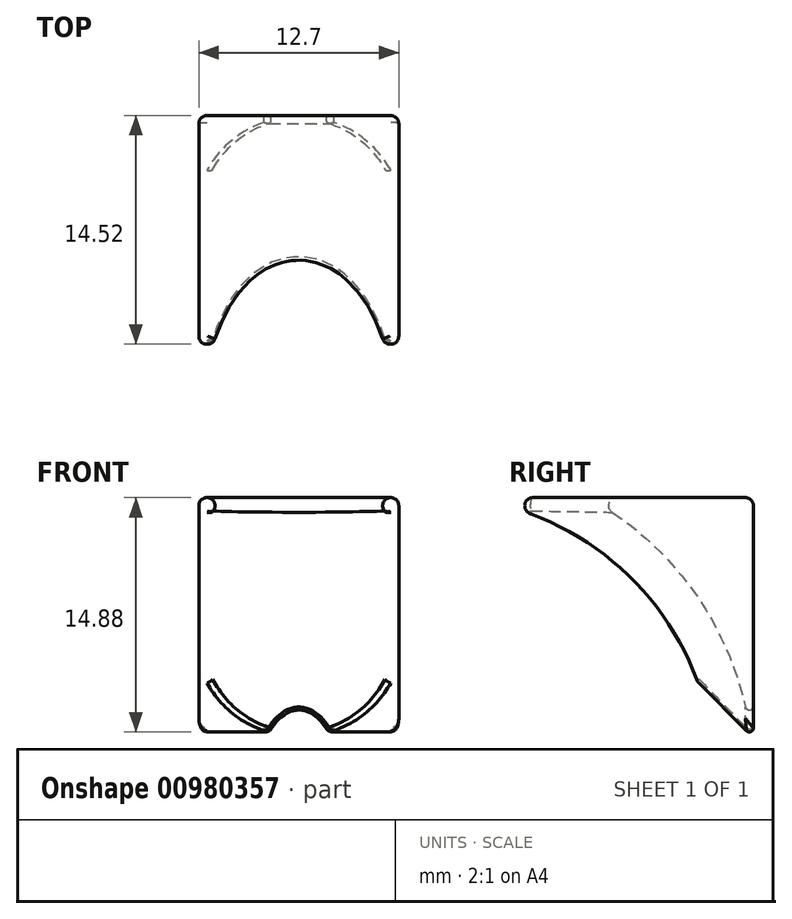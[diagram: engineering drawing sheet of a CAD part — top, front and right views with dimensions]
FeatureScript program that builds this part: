
annotation { "Feature Type Name" : "Feature", "Feature Type Description" : "" }
export const myFeature = defineFeature(function(context is Context, id is Id, definition is map)
    precondition{}
    {
        {
            var Q0;
            Q0=qCreatedBy(makeId("Right.planeOp"),FACE);
            var sketch = newSketch(context, id + "F0", { "sketchPlane" : qUnion([Q0])});
            skLineSegment(sketch, "E0", {"start": v(0, 0) * mm, "end": v(-15.24, 15.24) * mm});
            skLineSegment(sketch, "E1", {"start": v(-15.24, 15.24) * mm, "end": v(0, 15.24) * mm});
            skLineSegment(sketch, "E2", {"start": v(0, 15.24) * mm, "end": v(0, 0) * mm});
            skSolve(sketch);
        }
        {
            var Q0;
            Q0=makeQuery(id+"F0.imprint","IMPRINT",FACE,{"disambiguationData":[TD([[makeQuery(id+"F0.imprint","IMPRINT",EDGE,{"derivedFrom":sQuery(id+"F0.wireOp",EDGE,"E0")}),-1.0]])]});
            extrude(context, id + "F1", {"entities" : qUnion([Q0]), "endBound" : BoundingType.SYMMETRIC, "depth" : 12.7 * mm, "offsetDistance" : 25.4 * mm});
        }
        {
            var Q0;
            Q0=qCreatedBy(makeId("Top.planeOp"),FACE);
            cPlane(context, id + "F2", {"entities" : qUnion([Q0]), "cplaneType" : CPlaneType.OFFSET, "offset" : 2.54 * mm, "oppositeDirection" : true, "width" : 152.4 * mm, "height" : 152.4 * mm});
        }
        {
            var Q0;
            Q0=qCreatedBy(id+"F2.planeOp",FACE);
            var sketch = newSketch(context, id + "F3", { "sketchPlane" : qUnion([Q0])});
            skCircle(sketch, "E3", {"center": v(0, -7.62) * mm, "radius": 7.62 * mm});
            skLineSegment(sketch, "E4", {"start": v(-10.84, -20.32) * mm, "end": v(9.8, -20.32) * mm, "construction": true});
            skSolve(sketch);
        }
        {
            var Q0;
            Q0 = qSketchRegion(id + "F3", true);
            var Q1;
            Q1=sQuery(id+"F3.wireOp",EDGE,"E4");
            revolve(context, id + "F4", {"operationType" : NewBodyOperationType.REMOVE, "surfaceOperationType" : NewSurfaceOperationType.NEW, "entities" : qUnion([Q0]), "axis" : qUnion([Q1]), "revolveType" : RevolveType.FULL, "oppositeDirection" : true});
        }
        {
            var Q0;
            {var subQ0=sQuery(id+"F0.wireOp",EDGE,"E1");var subQ1=sQuery(id+"F0.wireOp",EDGE,"E0");Q0=makeQuery(id+"F4.boolean.opBoolean","SPLIT",FACE,{"disambiguationData":[TD([makeQuery(id+"F1.opExtrude","CAP_FACE",FACE,{"disambiguationData":[OSD([subQ1,subQ0,sQuery(id+"F0.wireOp",EDGE,"E2")])],"isStart":false}),makeQuery(id+"F1.opExtrude","SWEPT_FACE",FACE,{"disambiguationData":[OSD([subQ0])]}),makeQuery(id+"F4.opRevolve","SWEPT_FACE",FACE,{"disambiguationData":[OSD([sQuery(id+"F3.wireOp",EDGE,"E3")])]})])],"derivedFrom":makeQuery(id+"F1.opExtrude","SWEPT_FACE",FACE,{"disambiguationData":[OSD([subQ1])]})});}
            var Q1;
            {var subQ0=sQuery(id+"F0.wireOp",EDGE,"E1");var subQ1=sQuery(id+"F0.wireOp",EDGE,"E0");Q1=makeQuery(id+"F4.boolean.opBoolean","SPLIT",FACE,{"disambiguationData":[TD([makeQuery(id+"F1.opExtrude","CAP_FACE",FACE,{"disambiguationData":[OSD([subQ1,subQ0,sQuery(id+"F0.wireOp",EDGE,"E2")])],"isStart":true}),makeQuery(id+"F1.opExtrude","SWEPT_FACE",FACE,{"disambiguationData":[OSD([subQ0])]}),makeQuery(id+"F4.opRevolve","SWEPT_FACE",FACE,{"disambiguationData":[OSD([sQuery(id+"F3.wireOp",EDGE,"E3")])]})])],"derivedFrom":makeQuery(id+"F1.opExtrude","SWEPT_FACE",FACE,{"disambiguationData":[OSD([subQ1])]})});}
            var Q2;
            Q2=makeQuery(id+"F4.boolean.opBoolean","INTERSECT",EDGE,{"derivedFrom":[makeQuery(id+"F1.opExtrude","CAP_FACE",FACE,{"disambiguationData":[OSD([sQuery(id+"F0.wireOp",EDGE,"E0"),sQuery(id+"F0.wireOp",EDGE,"E1"),sQuery(id+"F0.wireOp",EDGE,"E2")])],"isStart":false}),makeQuery(id+"F4.opRevolve","SWEPT_FACE",FACE,{"disambiguationData":[OSD([sQuery(id+"F3.wireOp",EDGE,"E3")])]})]});
            var Q3;
            Q3=makeQuery(id+"F4.boolean.opBoolean","INTERSECT",EDGE,{"derivedFrom":[makeQuery(id+"F1.opExtrude","SWEPT_FACE",FACE,{"disambiguationData":[OSD([sQuery(id+"F0.wireOp",EDGE,"E1")])]}),makeQuery(id+"F4.opRevolve","SWEPT_FACE",FACE,{"disambiguationData":[OSD([sQuery(id+"F3.wireOp",EDGE,"E3")])]})]});
            var Q4;
            Q4=makeQuery(id+"F4.boolean.opBoolean","INTERSECT",EDGE,{"derivedFrom":[makeQuery(id+"F1.opExtrude","CAP_FACE",FACE,{"disambiguationData":[OSD([sQuery(id+"F0.wireOp",EDGE,"E0"),sQuery(id+"F0.wireOp",EDGE,"E1"),sQuery(id+"F0.wireOp",EDGE,"E2")])],"isStart":true}),makeQuery(id+"F4.opRevolve","SWEPT_FACE",FACE,{"disambiguationData":[OSD([sQuery(id+"F3.wireOp",EDGE,"E3")])]})]});
            var Q5;
            {var subQ0=sQuery(id+"F0.wireOp",EDGE,"E0");var subQ1=sQuery(id+"F0.wireOp",EDGE,"E2");Q5=makeQuery(id+"F4.boolean.opBoolean","SPLIT",EDGE,{"disambiguationData":[TD([makeQuery(id+"F1.opExtrude","SWEPT_FACE",FACE,{"disambiguationData":[OSD([subQ1])]})])],"derivedFrom":makeQuery(id+"F1.opExtrude","CAP_EDGE",EDGE,{"disambiguationData":[OSD([subQ0])],"isStart":false})});}
            var Q6;
            Q6=makeQuery(id+"F1.opExtrude","CAP_EDGE",EDGE,{"disambiguationData":[OSD([sQuery(id+"F0.wireOp",EDGE,"E2")])],"isStart":true});
            var Q7;
            {var subQ0=sQuery(id+"F0.wireOp",EDGE,"E0");var subQ1=sQuery(id+"F0.wireOp",EDGE,"E2");Q7=makeQuery(id+"F4.boolean.opBoolean","SPLIT",EDGE,{"disambiguationData":[TD([makeQuery(id+"F1.opExtrude","SWEPT_FACE",FACE,{"disambiguationData":[OSD([subQ1])]})])],"derivedFrom":makeQuery(id+"F1.opExtrude","CAP_EDGE",EDGE,{"disambiguationData":[OSD([subQ0])],"isStart":true})});}
            var Q8;
            Q8=makeQuery(id+"F1.opExtrude","CAP_EDGE",EDGE,{"disambiguationData":[OSD([sQuery(id+"F0.wireOp",EDGE,"E2")])],"isStart":false});
            var Q9;
            Q9=makeQuery(id+"F1.opExtrude","CAP_EDGE",EDGE,{"disambiguationData":[OSD([sQuery(id+"F0.wireOp",EDGE,"E1")])],"isStart":true});
            var Q10;
            Q10=makeQuery(id+"F1.opExtrude","CAP_EDGE",EDGE,{"disambiguationData":[OSD([sQuery(id+"F0.wireOp",EDGE,"E1")])],"isStart":false});
            var Q11;
            Q11=makeQuery(id+"F1.opExtrude","SWEPT_EDGE",EDGE,{"disambiguationData":[OSD([sQuery(id+"F0.wireOp",EDGE,"E1"),sQuery(id+"F0.wireOp",EDGE,"E2")])]});
            var Q12;
            Q12=makeQuery(id+"F4.boolean.opBoolean","INTERSECT",EDGE,{"disambiguationData":[OD(2.0)],"derivedFrom":[makeQuery(id+"F1.opExtrude","SWEPT_FACE",FACE,{"disambiguationData":[OSD([sQuery(id+"F0.wireOp",EDGE,"E0")])]}),makeQuery(id+"F4.opRevolve","SWEPT_FACE",FACE,{"disambiguationData":[OSD([sQuery(id+"F3.wireOp",EDGE,"E3")])]})]});
            fillet(context, id + "F5", {"entities" : qUnion([Q0, Q1, Q2, Q3, Q4, Q5, Q6, Q7, Q8, Q9, Q10, Q11, Q12]), "radius" : 0.5 * mm, "tangentPropagation" : true, "allowEdgeOverflow" : false});
        }
        {
            var Q0;
            Q0=makeQuery(id+"F1.opExtrude","SWEPT_EDGE",EDGE,{"disambiguationData":[OSD([sQuery(id+"F0.wireOp",EDGE,"E0"),sQuery(id+"F0.wireOp",EDGE,"E2")])]});
            fillet(context, id + "F6", {"entities" : qUnion([Q0]), "radius" : 0.25 * mm, "tangentPropagation" : true, "allowEdgeOverflow" : false});
        }
    });
